# Revit family: Franke_Refrigeration_side_unit_KE200_EC-A200_MS_EC(USA)
name_source: partatom
category: Specialty Equipment
revit_build: Autodesk Revit 2015 (Build: 20140606_1530(x64)
units: mm (PartAtom-declared; Revit-internal decimal feet)

## types (1)
- Refrigeration side unit  KE200 EC-A200 MS EC(110V/USA)
    Assembly Code = Refrigeration side unit
    Cost = 0 $
    Cycle = 60 Hz
    Cycle Alternative = 0 Hz
    Depth (mm) = 453 mm  [stored 1.48622 ft]
    Description = Refrigeration side unit for storage of cooled milk
    Energy loss acc. to DIN 18873 = 0.460 kWh/24 h - 230 V
    Height (mm) = 337 mm  [stored 1.10564 ft]
    Keynote = Refrigeration side unit
    Manufacturer = Franke
    Max Overcurrent Protection = 1.5 A
    Milk storage = 4 l
    Model = 410862 - Refrigeration side unit KE200 EC - A200 MS EC
    Number of Nutral Conductors = 1
    Number of Poles = 1
    Number of Protective Conductors = 1
    Temperature range = + 3°C to + 8°C
    URL = https://www.franke.com
    Volts max. = 0 V
    Volts min. = 110 V
    Watts = 0 W
    Weight = 13 kg
    Width (mm) = 225 mm  [stored 0.738189 ft]

note: [stored X ft] marks values corroborated as IEEE doubles in the binary element streams (Revit-internal decimal feet)

## geometry (parser evidence)
native form markers: Extrusion x1
no freeform markers — native parametric forms only
